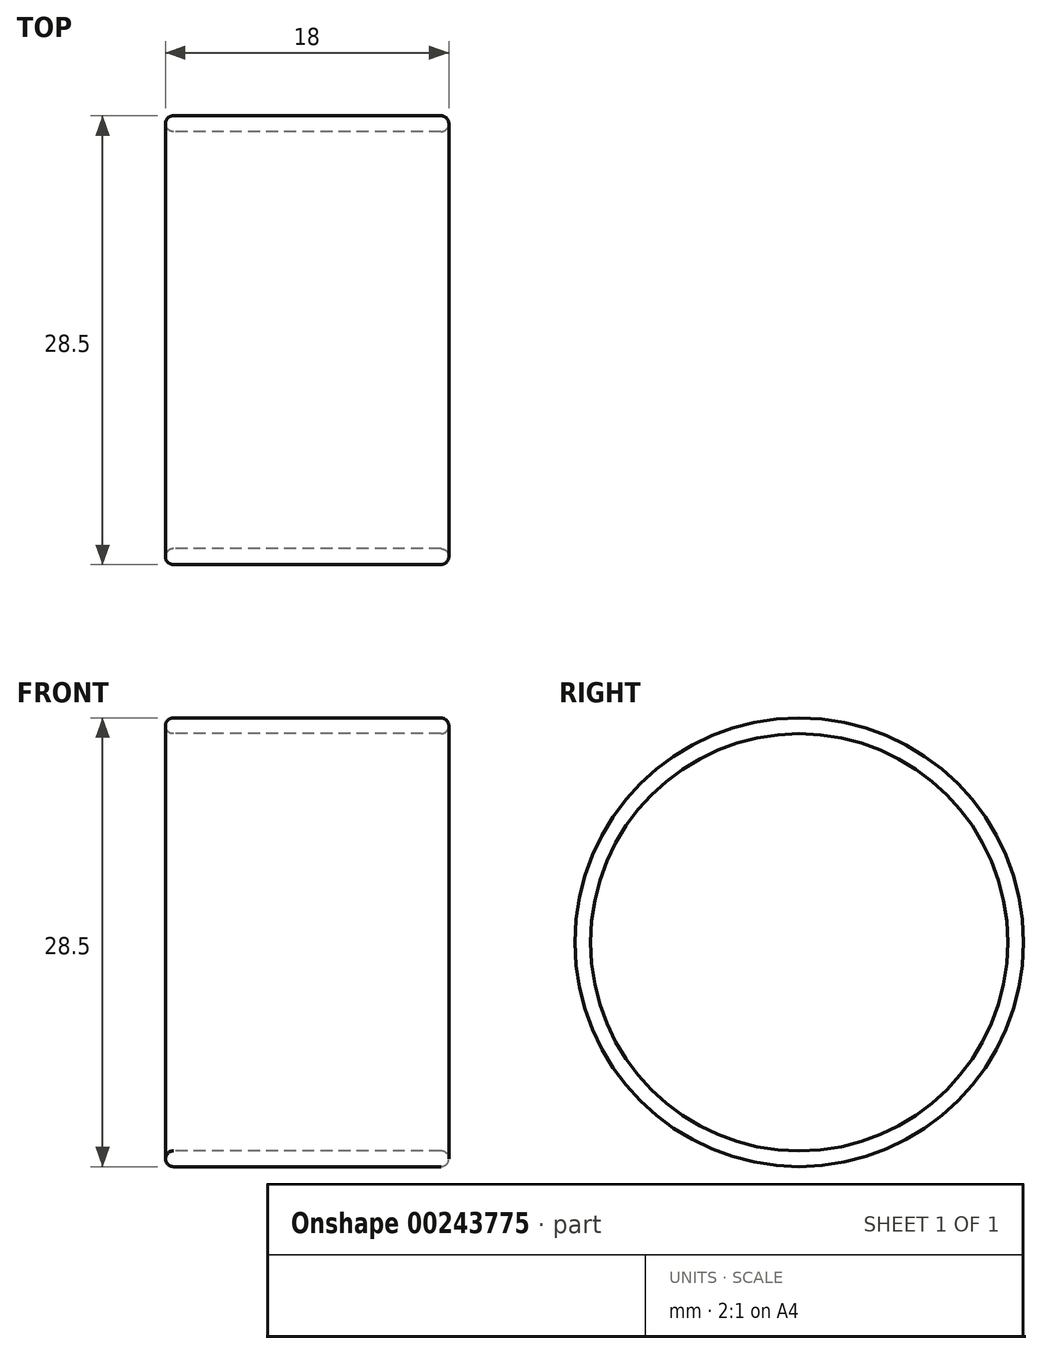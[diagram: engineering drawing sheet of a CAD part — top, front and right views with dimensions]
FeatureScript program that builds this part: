
annotation { "Feature Type Name" : "Feature", "Feature Type Description" : "" }
export const myFeature = defineFeature(function(context is Context, id is Id, definition is map)
    precondition{}
    {
        {
            var Q0;
            Q0=qCreatedBy(makeId("Front.planeOp"),FACE);
            var sketch = newSketch(context, id + "F0", { "sketchPlane" : qUnion([Q0])});
            skLineSegment(sketch, "E0.bottom", {"start": v(0, 14.25) * mm, "end": v(-18, 14.25) * mm});
            skLineSegment(sketch, "E0.top", {"start": v(0, 13.25) * mm, "end": v(-18, 13.25) * mm});
            skLineSegment(sketch, "E0.left", {"start": v(0, 14.25) * mm, "end": v(0, 13.25) * mm});
            skLineSegment(sketch, "E0.right", {"start": v(-18, 14.25) * mm, "end": v(-18, 13.25) * mm});
            skLineSegment(sketch, "E1", {"start": v(-26.62, 0) * mm, "end": v(10.2, 0) * mm, "construction": true});
            skSolve(sketch);
        }
        {
            var Q0;
            Q0=makeQuery(id+"F0.imprint","IMPRINT",FACE,{"disambiguationData":[TD([[makeQuery(id+"F0.imprint","IMPRINT",EDGE,{"derivedFrom":sQuery(id+"F0.wireOp",EDGE,"E0.bottom")}),1.0]])]});
            var Q1;
            Q1=sQuery(id+"F0.wireOp",EDGE,"E1");
            revolve(context, id + "F1", {"entities" : qUnion([Q0]), "axis" : qUnion([Q1]), "revolveType" : RevolveType.FULL});
        }
        {
            var Q0;
            Q0=makeQuery(id+"F1.opRevolve","SWEPT_FACE",FACE,{"disambiguationData":[OSD([sQuery(id+"F0.wireOp",EDGE,"E0.left")])]});
            fillet(context, id + "F2", {"entities" : qUnion([Q0]), "radius" : 0.5 * mm, "tangentPropagation" : true, "allowEdgeOverflow" : false});
        }
        {
            var Q0;
            Q0=makeQuery(id+"F1.opRevolve","SWEPT_FACE",FACE,{"disambiguationData":[OSD([sQuery(id+"F0.wireOp",EDGE,"E0.right")])]});
            fillet(context, id + "F3", {"entities" : qUnion([Q0]), "radius" : 0.5 * mm, "tangentPropagation" : true, "allowEdgeOverflow" : false});
        }
    });
